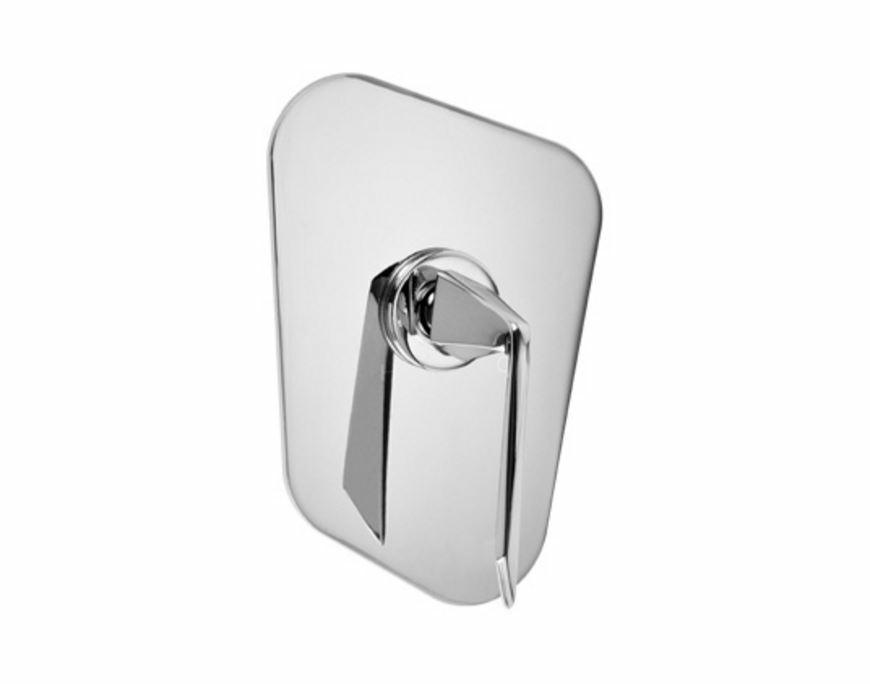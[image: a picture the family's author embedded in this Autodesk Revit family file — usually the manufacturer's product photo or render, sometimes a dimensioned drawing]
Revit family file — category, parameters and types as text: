
# Revit family: PIU-200_RFA
name_source: partatom
category: Aparatos sanitarios
units: mm (PartAtom-declared; Revit-internal decimal feet)

## family parameters
Compartido = Sí
Corte con vacíos al cargar = No
Cota de conector redondo = Diámetro de uso
Número OmniClass = 23.45.05.14.99
Punto de cálculo de habitación = Sí
Se basa en plano de trabajo = Sí
Siempre vertical = Sí
Tipo de pieza = Normal
Título OmniClass = Other Sanitary Washing Plumbing Fixtures

## types (1)
- PIU-200
    Brass Chromed = Brass
    Cartucho = Cartucho monomando cerámico  Ø40mm
    Comentarios de tipo = Monomando Piura
    Descripción = Monomando para Regadera sin Balanceo de Presión sin Desviador
    Elevación por defecto = 1"
    Fabricante = HELVEX S.A. DE C.V.
    Garantía = El producto HELVEX está garantizado como libre de defectos en materiales y procesos de fabricación. El producto HELVEX está garantizado, en lo que se refiere a los acabados; por un periodo de 10 años en los acabados cromo y duravex, y por 2 años en cabados diferentes al cromo, a partir de la fecha de compra indicada en la factura.
    Imagen de tipo = PIU-200.JPG
    Instalación = ½" - 14 NPT
    Modelo = PIU-200
    Operación = Para abrir el flujo de agua levante la palanca maneral y gire para regular la temperatura.
    Presión máxima de trabajo = 85.3 psi
    Presión mínima de trabajo = 14.2 psi
    Support Base Diameter = 5"
    Total Height = 8"
    URL = http://www.helvex.com.mx

## geometry (parser evidence)
native form markers: Sweep x3
no freeform markers — native parametric forms only
